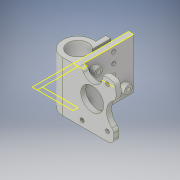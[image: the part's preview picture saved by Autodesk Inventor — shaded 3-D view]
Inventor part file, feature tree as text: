
AUTODESK INVENTOR PART (.ipt)
format: ipt  version: 2018 (Build 220112000, 112)  size: 218,624 bytes
history: native  units: in
note: dims shown in document units (in); Inventor stores cm internally (conversion verified against a paired STEP export)
features: sketch x8, other x3
ambient origin geometry x8: Origin, YZ Plane, XZ Plane, XY Plane, X Axis, Y Axis, Z Axis, Center Point
bodies: Solid1 (feature_tree)
feature tree (11):
  other  "motor mount 2.ipt"
  other  "Solid1::motor mount 2.ipt"
  other  "TaggingFeature1"
  sketch  "Sketch1"  dims[d0=0.3937in]
  sketch  "Sketch2"
  sketch  "Sketch4"
  sketch  "Sketch3"
  sketch  "Sketch5"
  sketch  "Sketch6"
  sketch  "Sketch7"
  sketch  "Sketch8"
